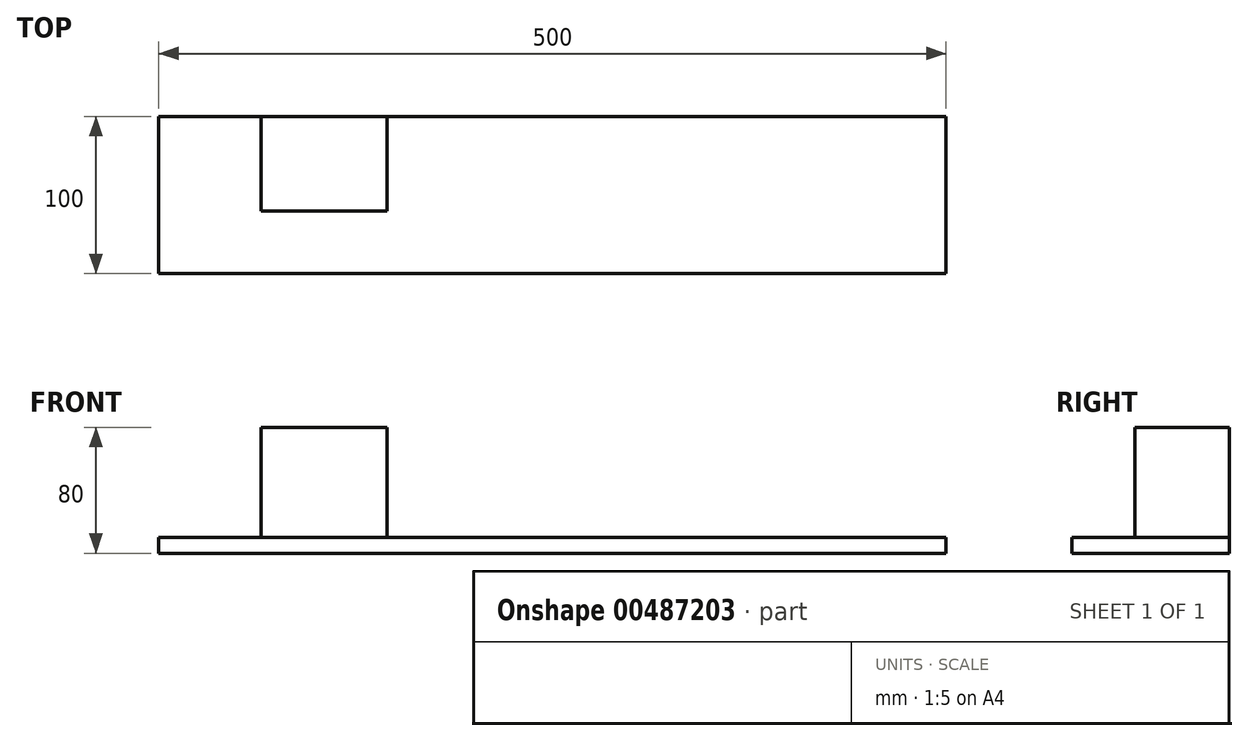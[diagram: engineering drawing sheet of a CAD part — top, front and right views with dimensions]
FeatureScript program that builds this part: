
annotation { "Feature Type Name" : "Feature", "Feature Type Description" : "" }
export const myFeature = defineFeature(function(context is Context, id is Id, definition is map)
    precondition{}
    {
        {
            var Q0;
            Q0=qCreatedBy(makeId("Front.planeOp"),FACE);
            var sketch = newSketch(context, id + "F0", { "sketchPlane" : qUnion([Q0])});
            skLineSegment(sketch, "E0.bottom", {"start": v(0, 57.97) * mm, "end": v(0, 57.97) * mm});
            skLineSegment(sketch, "E0.top", {"start": v(0, 131.88) * mm, "end": v(0, 131.88) * mm});
            skLineSegment(sketch, "E0.left", {"start": v(0, 57.97) * mm, "end": v(0, 131.88) * mm});
            skLineSegment(sketch, "E0.right", {"start": v(0, 57.97) * mm, "end": v(0, 131.88) * mm});
            skLineSegment(sketch, "E1.bottom", {"start": v(500, 10) * mm, "end": v(0, 10) * mm});
            skLineSegment(sketch, "E1.top", {"start": v(500, 0) * mm, "end": v(0, 0) * mm});
            skLineSegment(sketch, "E1.left", {"start": v(500, 10) * mm, "end": v(500, 0) * mm});
            skLineSegment(sketch, "E1.right", {"start": v(0, 10) * mm, "end": v(0, 0) * mm});
            skSolve(sketch);
        }
        {
            var Q0;
            Q0 = qSketchRegion(id + "F0", true);
            extrude(context, id + "F1", {"entities" : qUnion([Q0]), "depth" : 100 * mm});
        }
        {
            var Q0;
            Q0=qCreatedBy(makeId("Front.planeOp"),FACE);
            var sketch = newSketch(context, id + "F2", { "sketchPlane" : qUnion([Q0])});
            skLineSegment(sketch, "E2.bottom", {"start": v(144.87, 80) * mm, "end": v(64.87, 80) * mm});
            skLineSegment(sketch, "E2.top", {"start": v(144.87, 0) * mm, "end": v(64.87, 0) * mm});
            skLineSegment(sketch, "E2.left", {"start": v(144.87, 80) * mm, "end": v(144.87, 0) * mm});
            skLineSegment(sketch, "E2.right", {"start": v(64.87, 80) * mm, "end": v(64.87, 0) * mm});
            skSolve(sketch);
        }
        {
            var Q0;
            Q0=sQuery(id+"F2.wireOp",EDGE,"E2.bottom");
            extrude(context, id + "F3", {"bodyType" : ToolBodyType.SURFACE, "surfaceEntities" : qUnion([Q0]), "depth" : 60 * mm});
        }
        {
            var Q0;
            Q0=makeQuery(id+"F3.opExtrude","SWEPT_FACE",FACE,{"disambiguationData":[OSD([sQuery(id+"F2.wireOp",EDGE,"E2.bottom")])]});
            extrude(context, id + "F4", {"entities" : qUnion([Q0]), "operationType" : NewBodyOperationType.ADD, "oppositeDirection" : true, "depth" : 80 * mm});
        }
    });
